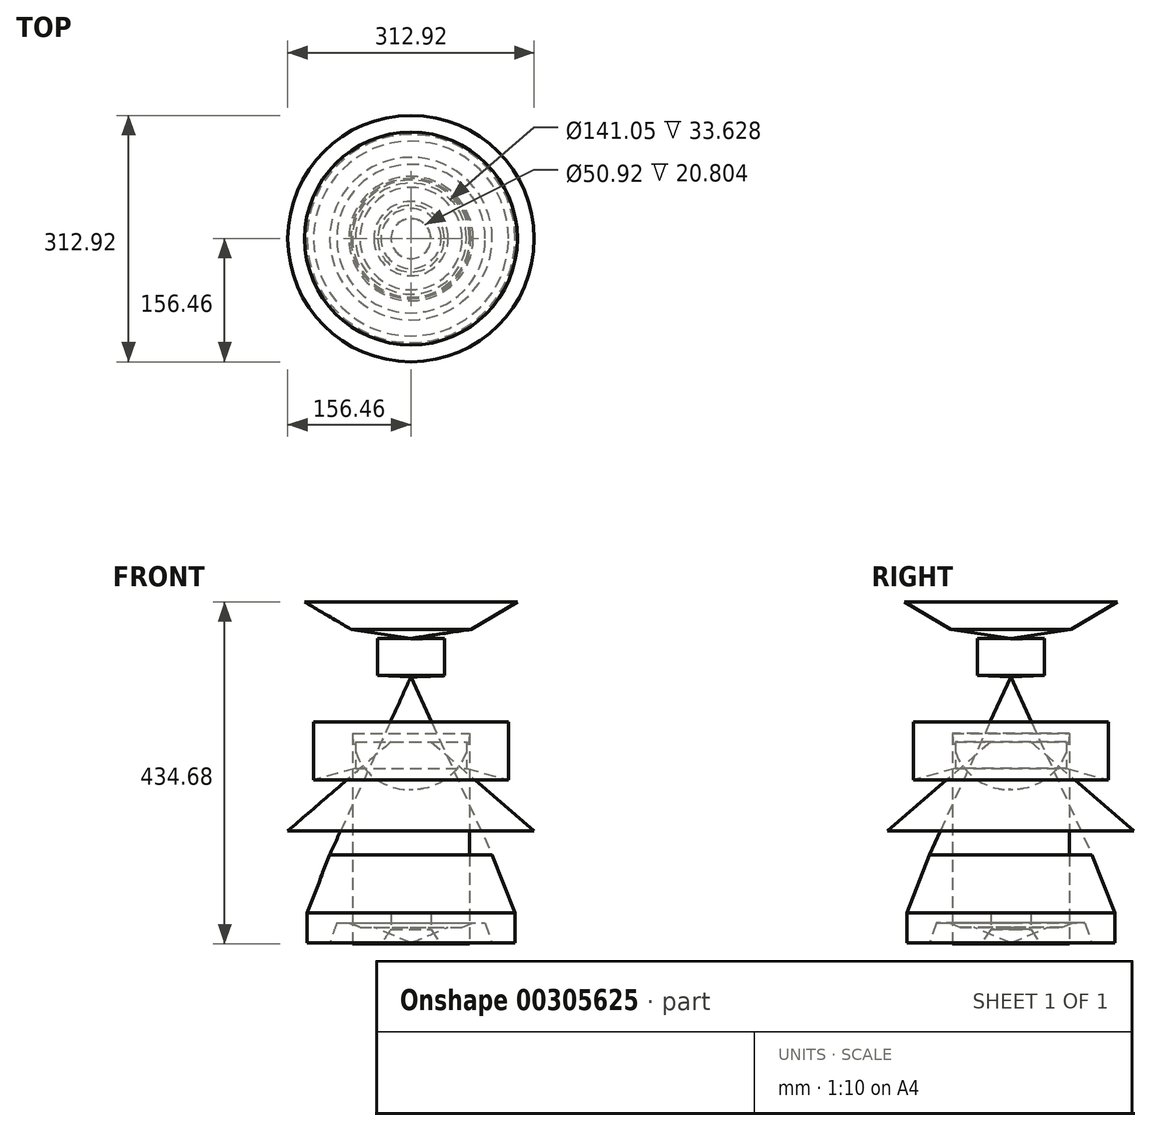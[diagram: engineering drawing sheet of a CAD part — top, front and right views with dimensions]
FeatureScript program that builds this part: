
annotation { "Feature Type Name" : "Feature", "Feature Type Description" : "" }
export const myFeature = defineFeature(function(context is Context, id is Id, definition is map)
    precondition{}
    {
        {
            var Q0;
            Q0=qCreatedBy(makeId("Front.planeOp"),FACE);
            var sketch = newSketch(context, id + "F0", { "sketchPlane" : qUnion([Q0])});
            skLineSegment(sketch, "E0", {"start": v(0, 0) * mm, "end": v(0, 300) * mm});
            skLineSegment(sketch, "E1", {"start": v(0, 0) * mm, "end": v(25.46, 0) * mm});
            skLineSegment(sketch, "E2", {"start": v(25.46, 0) * mm, "end": v(25.46, -20.8) * mm});
            skLineSegment(sketch, "E3", {"start": v(25.46, -20.8) * mm, "end": v(38.1, -39.33) * mm});
            skLineSegment(sketch, "E4", {"start": v(38.1, -39.33) * mm, "end": v(74.3, -39.33) * mm});
            skLineSegment(sketch, "E5", {"start": v(74.3, -39.33) * mm, "end": v(74.3, 228.48) * mm});
            skArc(sketch, "E6", {"start": v(74.3, 228.48) * mm, "mid": v(52.37, 280.05) * mm, "end": v(0, 300) * mm});
            skLineSegment(sketch, "E7", {"start": v(0, 300) * mm, "end": v(42.37, 301.62) * mm});
            skLineSegment(sketch, "E8", {"start": v(42.37, 348.9) * mm, "end": v(42.37, 301.62) * mm});
            skLineSegment(sketch, "E9", {"start": v(42.37, 348.9) * mm, "end": v(0, 347.29) * mm});
            skLineSegment(sketch, "E10", {"start": v(0, 347.29) * mm, "end": v(0, 300) * mm});
            skSolve(sketch);
        }
        {
            var Q0;
            Q0 = qSketchRegion(id + "F0", true);
            var Q1;
            Q1=sQuery(id+"F0.wireOp",EDGE,"E0");
            revolve(context, id + "F1", {"entities" : qUnion([Q0]), "axis" : qUnion([Q1]), "revolveType" : RevolveType.FULL});
        }
        {
            var Q0;
            Q0=qCreatedBy(makeId("Front.planeOp"),FACE);
            var sketch = newSketch(context, id + "F2", { "sketchPlane" : qUnion([Q0])});
            skLineSegment(sketch, "E11", {"start": v(0, 0) * mm, "end": v(0, 74.14) * mm});
            skLineSegment(sketch, "E12", {"start": v(0, 74.14) * mm, "end": v(103.22, 74.14) * mm});
            skLineSegment(sketch, "E13", {"start": v(103.22, 74.14) * mm, "end": v(103.22, 0) * mm});
            skLineSegment(sketch, "E14", {"start": v(103.22, 0) * mm, "end": v(0, 0) * mm});
            skLineSegment(sketch, "E15", {"start": v(0, 74.14) * mm, "end": v(0, 300.19) * mm});
            skLineSegment(sketch, "E16", {"start": v(0, 300.19) * mm, "end": v(103.22, 74.14) * mm});
            skLineSegment(sketch, "E17", {"start": v(0, 0) * mm, "end": v(0, -37.96) * mm});
            skLineSegment(sketch, "E18", {"start": v(0, -37.96) * mm, "end": v(47.17, -17.87) * mm});
            skLineSegment(sketch, "E19", {"start": v(47.17, -17.87) * mm, "end": v(64.92, -17.87) * mm});
            skLineSegment(sketch, "E20", {"start": v(64.92, -17.87) * mm, "end": v(78.93, -12.74) * mm});
            skLineSegment(sketch, "E21", {"start": v(78.93, -12.74) * mm, "end": v(94.35, -12.74) * mm});
            skLineSegment(sketch, "E22", {"start": v(94.35, -12.74) * mm, "end": v(103.22, -37.96) * mm});
            skLineSegment(sketch, "E23", {"start": v(103.22, -37.96) * mm, "end": v(132.18, -37.96) * mm});
            skLineSegment(sketch, "E24", {"start": v(132.18, -37.96) * mm, "end": v(132.18, 0) * mm});
            skLineSegment(sketch, "E25", {"start": v(132.18, 0) * mm, "end": v(103.22, 0) * mm});
            skLineSegment(sketch, "E26", {"start": v(132.18, 0) * mm, "end": v(103.22, 74.14) * mm});
            skSolve(sketch);
        }
        {
            var Q0;
            Q0 = qSketchRegion(id + "F2", true);
            var Q1;
            Q1=sQuery(id+"F2.wireOp",EDGE,"E15");
            revolve(context, id + "F3", {"entities" : qUnion([Q0]), "axis" : qUnion([Q1]), "revolveType" : RevolveType.FULL});
        }
        {
            var Q0;
            Q0=qCreatedBy(makeId("Front.planeOp"),FACE);
            var sketch = newSketch(context, id + "F4", { "sketchPlane" : qUnion([Q0])});
            skLineSegment(sketch, "E27", {"start": v(0, 0) * mm, "end": v(0, 242.74) * mm});
            skLineSegment(sketch, "E28", {"start": v(0, 242.74) * mm, "end": v(-123.77, 242.74) * mm});
            skLineSegment(sketch, "E29", {"start": v(-123.77, 242.74) * mm, "end": v(-123.77, 168.95) * mm});
            skLineSegment(sketch, "E30", {"start": v(-123.77, 168.95) * mm, "end": v(-70.53, 183.9) * mm});
            skLineSegment(sketch, "E31", {"start": v(-70.53, 183.9) * mm, "end": v(-70.53, 217.52) * mm});
            skLineSegment(sketch, "E32", {"start": v(-70.53, 217.52) * mm, "end": v(-25.22, 217.52) * mm});
            skLineSegment(sketch, "E33", {"start": v(-25.22, 217.52) * mm, "end": v(-156.46, 104.5) * mm});
            skLineSegment(sketch, "E34", {"start": v(-156.46, 104.5) * mm, "end": v(0, 104.5) * mm});
            skSolve(sketch);
        }
        {
            var Q0;
            Q0 = qSketchRegion(id + "F4", true);
            var Q1;
            Q1=sQuery(id+"F4.wireOp",EDGE,"E27");
            revolve(context, id + "F5", {"entities" : qUnion([Q0]), "axis" : qUnion([Q1]), "revolveType" : RevolveType.FULL});
        }
        {
            var Q0;
            Q0=qCreatedBy(makeId("Front.planeOp"),FACE);
            var sketch = newSketch(context, id + "F6", { "sketchPlane" : qUnion([Q0])});
            skLineSegment(sketch, "E35", {"start": v(0, 0) * mm, "end": v(0, 395.35) * mm});
            skLineSegment(sketch, "E36", {"start": v(0, 395.35) * mm, "end": v(135.19, 395.35) * mm});
            skLineSegment(sketch, "E37", {"start": v(135.19, 395.35) * mm, "end": v(76.22, 360.48) * mm});
            skLineSegment(sketch, "E38", {"start": v(76.22, 360.48) * mm, "end": v(0, 349.07) * mm});
            skSolve(sketch);
        }
        {
            var Q0;
            Q0 = qSketchRegion(id + "F6", true);
            var Q1;
            Q1=sQuery(id+"F6.wireOp",EDGE,"E35");
            revolve(context, id + "F7", {"entities" : qUnion([Q0]), "axis" : qUnion([Q1]), "revolveType" : RevolveType.FULL});
        }
    });
